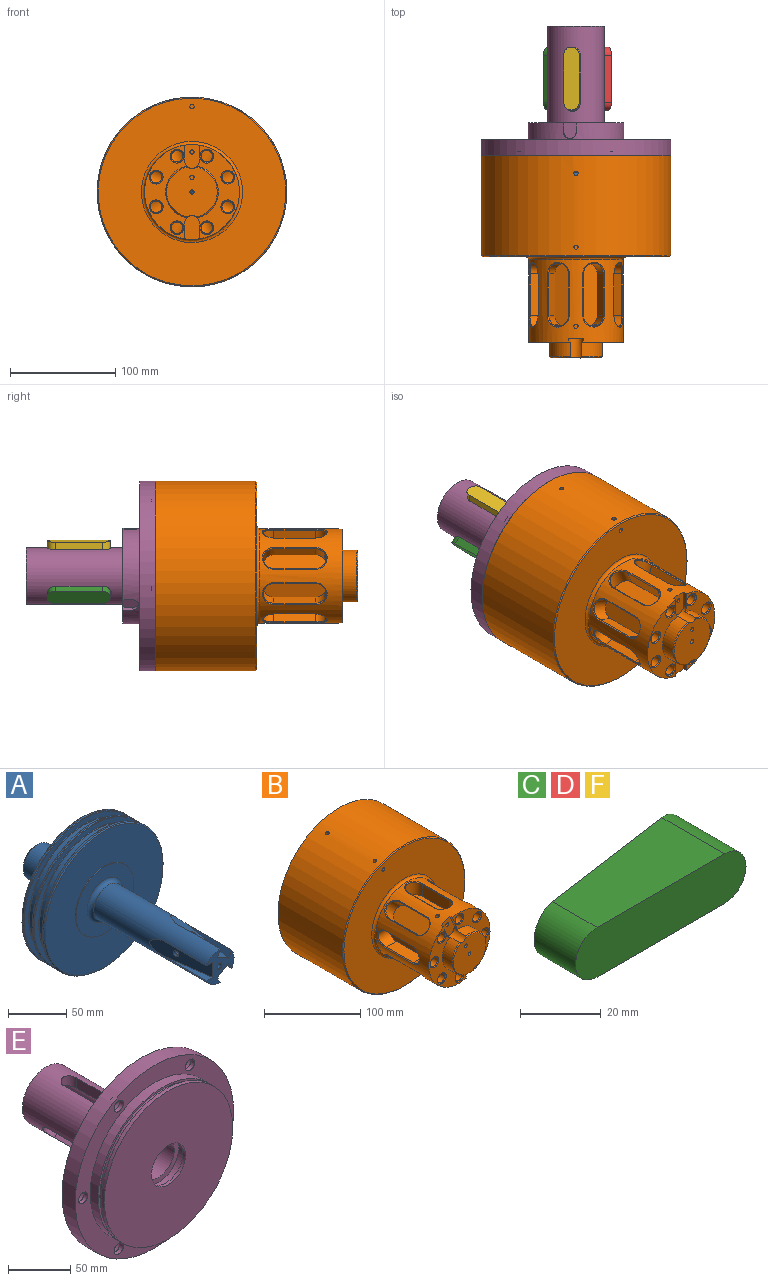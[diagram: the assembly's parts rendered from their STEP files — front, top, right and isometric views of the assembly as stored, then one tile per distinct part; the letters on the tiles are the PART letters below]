
ASSEMBLY  parts=6 mates=5
PART A: 68 faces, bbox 145x224.3x145 mm
  f0: cylinder r=1.5mm len=26.28mm, axis (0,-1,0), area 245.5mm2, adj f1,f2,f3,f4,f5,f6,f65
  f1: cylinder r=1.5mm len=11.87mm, axis (-0.99,-0.14,0), area 97.1mm2, adj f0,f4,f6,f51
  f2: cylinder r=1.5mm len=11.46mm, axis (0.5,-0.14,0.86), area 97.1mm2, adj f0,f3,f6,f55
  f3: cylinder r=1.5mm len=6.5mm, axis (-0.99,-0.14,0), area 44.4mm2, adj f0,f2,f4,f5,f6,f56
  f4: cylinder r=1.5mm len=6.81mm, axis (0.5,-0.14,0.86), area 44.4mm2, adj f0,f1,f3,f5,f6,f57
  f5: cylinder r=1.5mm len=11.46mm, axis (0.5,-0.14,-0.86), area 97.1mm2, adj f0,f3,f4,f61
  f6: cylinder r=1.5mm len=6.81mm, axis (0.5,-0.14,-0.86), area 44.4mm2, adj f0,f1,f2,f3,f4,f62
  f7: cylinder r=17.48mm len=135mm, axis (0,1,0), area 11728.8mm2, adj f8,f48,f49,f50,f52,f53,f54,f58
  f8: plane 34.95x33.06mm, normal (0,-1,0), area 511.1mm2, adj f7,f48,f49,f50,f52,f53,f54,f58
  f9: cylinder r=1.5mm len=17.25mm, axis (0,0,-1), area 153.3mm2, adj f10,f32,f36
  f10: cylinder r=17.25mm len=34.5mm, axis (0,-1,0), area 2594.2mm2, adj f9,f29,f64
  f11: cylinder r=72.5mm len=145mm, axis (0,1,0), area 774.4mm2, adj f39,f40
  f12: plane 143x143mm, normal (0,-1,0), area 12212.2mm2, adj f26,f39
  f13: plane 144x144mm, normal (0,-1,0), area 2393.1mm2, adj f42,f43
  f14: plane 144x144mm, normal (0,1,0), area 2393.1mm2, adj f40,f41
  f15: cylinder r=66mm len=132mm, axis (0,-1,0), area 3524.9mm2, adj f41,f42
  f16: cylinder r=72.5mm len=145mm, axis (0,1,0), area 728.8mm2, adj f43,f44
  f17: plane 144x144mm, normal (0,-1,0), area 2393.1mm2, adj f46,f47
  f18: plane 144x144mm, normal (0,1,0), area 2393.1mm2, adj f44,f45
  f19: cylinder r=66mm len=132mm, axis (0,-1,0), area 3524.9mm2, adj f45,f46
  f20: cylinder r=72.5mm len=145mm, axis (0,1,0), area 774.4mm2, adj f38,f47
  f21: plane 143x143mm, normal (0,1,0), area 2582.4mm2, adj f22,f38
  f22: cylinder r=65.5mm len=131mm, axis (0,-1,0), area 535mm2, adj f21,f23
  f23: plane 131x131mm, normal (0,1,0), area 3091.3mm2, adj f22,f24
  f24: cylinder r=57.5mm len=115mm, axis (0,1,0), area 2529mm2, adj f23,f25
  f25: plane 115x115mm, normal (0,1,0), area 9098.6mm2, adj f24,f64
  f26: cylinder r=35mm len=70mm, axis (0,1,0), area 219.9mm2, adj f12,f27
  f27: plane 70x70mm, normal (0,-1,0), area 2399.6mm2, adj f26,f63
  f28: cylinder r=17.48mm len=34.95mm, axis (0,1,0), area 3403.8mm2, adj f29,f31
  f29: plane 34.95x34.95mm, normal (0,-1,0), area 24.5mm2, adj f10,f28
  f30: plane 26.95x26.95mm, normal (0,1,0), area 550.8mm2, adj f31,f33
  f31: cone r=13.48mm half-angle=45deg, axis (0,-1,0), area 550mm2, adj f28,f30
  f32: cylinder r=1.5mm len=56mm, axis (0,1,0), area 518.8mm2, adj f9,f33,f35
  f33: cone r=1.5mm half-angle=45deg, axis (0,1,0), area 17.8mm2, adj f30,f32
  f34: cone r=0mm half-angle=59deg, axis (0,0,-1), area 8.2mm2, adj f35
  f35: cylinder r=1.5mm len=3mm, axis (0,0,-1), area 17.5mm2, adj f32,f34,f36
  f36: cylinder r=1.5mm len=13mm, axis (0,1,0), area 113.5mm2, adj f9,f35,f37
  f37: cone r=0mm half-angle=59deg, axis (0,1,0), area 8.2mm2, adj f36
  f38: cone r=72.5mm half-angle=45deg, axis (0,-1,0), area 639.8mm2, adj f20,f21
  f39: cone r=71.5mm half-angle=45deg, axis (0,1,0), area 639.8mm2, adj f11,f12
  f40: cone r=72.5mm half-angle=45deg, axis (0,-1,0), area 321mm2, adj f11,f14
  f41: cone r=66.5mm half-angle=45deg, axis (0,-1,0), area 294.3mm2, adj f14,f15
  f42: cone r=66mm half-angle=45deg, axis (0,1,0), area 294.3mm2, adj f13,f15
  f43: cone r=72mm half-angle=45deg, axis (0,1,0), area 321mm2, adj f13,f16
  f44: cone r=72.5mm half-angle=45deg, axis (0,-1,0), area 321mm2, adj f16,f18
  f45: cone r=66.5mm half-angle=45deg, axis (0,-1,0), area 294.3mm2, adj f18,f19
  f46: cone r=66mm half-angle=45deg, axis (0,1,0), area 294.3mm2, adj f17,f19
  f47: cone r=72mm half-angle=45deg, axis (0,1,0), area 321mm2, adj f17,f20
  f48: plane 53.99x7.59mm, normal (0,0,1), area 204.8mm2, adj f7,f8,f50
  f49: plane 53.99x7.59mm, normal (0,0,-1), area 204.8mm2, adj f7,f8,f50
  f50: plane 67.42x15.8mm, normal (-0.99,-0.14,0), area 977.6mm2, adj f7,f8,f48,f49,f51
  f51: cone r=1.5mm half-angle=45deg, axis (-0.99,-0.14,0), area 30mm2, adj f1,f50
  f52: plane 53.99x6.57mm, normal (0.87,0,-0.5), area 204.8mm2, adj f7,f8,f54
  f53: plane 53.99x6.57mm, normal (-0.87,0,0.5), area 204.8mm2, adj f7,f8,f54
  f54: plane 67.42x17.48mm, normal (0.5,-0.14,0.86), area 977.6mm2, adj f7,f8,f52,f53,f55
  f55: cone r=1.5mm half-angle=45deg, axis (0.5,-0.14,0.86), area 30mm2, adj f2,f54
  f56: cone r=0mm half-angle=59deg, axis (-0.99,-0.14,0), area 8.2mm2, adj f3
  f57: cone r=0mm half-angle=59deg, axis (0.5,-0.14,0.86), area 8.2mm2, adj f4
  f58: plane 53.99x6.57mm, normal (-0.87,0,-0.5), area 204.8mm2, adj f7,f8,f60
  f59: plane 53.99x6.57mm, normal (0.87,0,0.5), area 204.8mm2, adj f7,f8,f60
  f60: plane 67.42x17.48mm, normal (0.5,-0.14,-0.86), area 977.6mm2, adj f7,f8,f58,f59,f61
  f61: cone r=1.5mm half-angle=45deg, axis (0.5,-0.14,-0.86), area 30mm2, adj f5,f60
  f62: cone r=0mm half-angle=59deg, axis (0.5,-0.14,-0.86), area 8.2mm2, adj f6
  f63: torus R=21.48mm, axis (0,-1,0), area 747.3mm2, adj f7,f27
  f64: torus R=20.25mm, axis (0,1,0), area 543mm2, adj f10,f25
  f65: cone r=0mm half-angle=59deg, axis (0,-1,0), area 14.7mm2, adj f0,f66
  f66: cylinder r=2.5mm len=12.5mm, axis (0,-1,0), area 196.3mm2, adj f65,f67
  f67: cone r=2.5mm half-angle=45deg, axis (0,-1,0), area 12.2mm2, adj f8,f66
PART B: 156 faces, bbox 180x192x180 mm
  f0: cylinder r=2mm len=7.96mm, axis (-0.38,0,0.92), area 87.4mm2, adj f11,f123,f128
  f1: cylinder r=2mm len=41.26mm, axis (-0.38,0,0.92), area 510.5mm2, adj f2,f122,f123,f127
  f2: cylinder r=2mm len=9mm, axis (0,-1,0), area 99.3mm2, adj f1,f7,f121
  f3: cylinder r=2mm len=30mm, axis (0,-1,0), area 377mm2, adj f14,f112,f115
  f4: plane 83.39x55.54mm, normal (0,-1,0), area 1392.8mm2, adj f5,f11,f69,f80,f91,f102,f105,f106
  f5: cylinder r=25mm len=45.67mm, axis (0,1,0), area 956.4mm2, adj f4,f106,f110,f135
  f6: cylinder r=90mm len=180mm, axis (0,1,0), area 53695.6mm2, adj f9,f117,f121,f155
  f7: plane 178x178mm, normal (0,-1,0), area 17633.8mm2, adj f2,f134,f155
  f8: cylinder r=73mm len=146mm, axis (0,-1,0), area 30260.1mm2, adj f120,f132,f133
  f9: plane 180x180mm, normal (0,1,0), area 7304.2mm2, adj f6,f132,f138,f141,f144,f147,f150,f153
  f10: plane 140x140mm, normal (0,1,0), area 14318.6mm2, adj f131,f133
  f11: cylinder r=45mm len=90mm, axis (0,1,0), area 11744.7mm2, adj f0,f4,f12,f20,f21,f22,f23,f31
  f12: plane 83.39x55.54mm, normal (0,-1,0), area 1392.8mm2, adj f11,f13,f25,f36,f47,f58,f104,f106
  f13: cylinder r=25mm len=45.67mm, axis (0,1,0), area 956.4mm2, adj f12,f106,f110,f136
  f14: plane 48x48mm, normal (0,-1,0), area 1765.4mm2, adj f3,f106,f110,f111,f135,f136
  f15: cylinder r=10.1mm len=20.2mm, axis (0,0,1), area 470.9mm2, adj f16,f18,f19,f20
  f16: plane 39.8x14.84mm, normal (1,0,0), area 590.6mm2, adj f15,f17,f19,f22
  f17: cylinder r=10.1mm len=20.2mm, axis (0,0,1), area 371.8mm2, adj f16,f18,f19,f23,f24
  f18: plane 39.8x14.84mm, normal (-1,0,0), area 590.6mm2, adj f15,f17,f19,f21
  f19: plane 60x20.2mm, normal (0,0,1), area 1124.4mm2, adj f15,f16,f17,f18
  f20: bspline ~22.19x10.89mm, area 39.7mm2, adj f11,f15,f21,f22
  f21: plane 39.8x0.99mm, normal (-0.61,0,0.79), area 50mm2, adj f11,f18,f20,f23
  f22: plane 39.8x0.99mm, normal (0.61,0,0.79), area 50mm2, adj f11,f16,f20,f23
  f23: bspline ~22.18x10.89mm, area 39.7mm2, adj f11,f17,f21,f22
  f24: cylinder r=5.5mm len=14mm, axis (0,-1,0), area 483.8mm2, adj f17,f25
  f25: cone r=5.5mm half-angle=45deg, axis (0,-1,0), area 53.3mm2, adj f12,f24
  f26: cylinder r=10.1mm len=24.78mm, axis (0.71,0,0.71), area 470.9mm2, adj f27,f29,f30,f31
  f27: plane 39.8x10.49mm, normal (0.71,0,-0.71), area 590.6mm2, adj f26,f28,f30,f33
  f28: cylinder r=10.1mm len=24.78mm, axis (0.71,0,0.71), area 371.8mm2, adj f27,f29,f30,f34,f35
  f29: plane 39.8x10.49mm, normal (-0.71,0,0.71), area 590.6mm2, adj f26,f28,f30,f32
  f30: plane 60x14.28mm, normal (0.71,0,0.71), area 1124.4mm2, adj f26,f27,f28,f29
  f31: bspline ~15.69x15.69mm, area 39.7mm2, adj f11,f26,f32,f33
  f32: plane 39.8x1.25mm, normal (0.12,0,0.99), area 50mm2, adj f11,f29,f31,f34
  f33: plane 39.8x1.25mm, normal (0.99,0,0.12), area 50mm2, adj f11,f27,f31,f34
  f34: bspline ~15.69x15.69mm, area 39.7mm2, adj f11,f28,f32,f33
  f35: cylinder r=5.5mm len=14.78mm, axis (0,-1,0), area 510.7mm2, adj f28,f36
  f36: cone r=5.5mm half-angle=45deg, axis (0,-1,0), area 53.3mm2, adj f12,f35
  f37: cylinder r=10.1mm len=20.2mm, axis (1,0,0), area 470.9mm2, adj f38,f40,f41,f42
  f38: plane 39.8x14.84mm, normal (0,0,-1), area 590.6mm2, adj f37,f39,f41,f44
  f39: cylinder r=10.1mm len=20.2mm, axis (1,0,0), area 371.8mm2, adj f38,f40,f41,f45,f46
  f40: plane 39.8x14.84mm, normal (0,0,1), area 590.6mm2, adj f37,f39,f41,f43
  f41: plane 60x20.2mm, normal (1,0,0), area 1124.4mm2, adj f37,f38,f39,f40
  f42: bspline ~22.18x10.9mm, area 39.7mm2, adj f11,f37,f43,f44
  f43: plane 39.8x0.99mm, normal (0.79,0,0.61), area 50mm2, adj f11,f40,f42,f45
  f44: plane 39.8x0.99mm, normal (0.79,0,-0.61), area 50mm2, adj f11,f38,f42,f45
  f45: bspline ~22.18x10.9mm, area 39.7mm2, adj f11,f39,f43,f44
  f46: cylinder r=5.5mm len=15.63mm, axis (0,-1,0), area 540.1mm2, adj f39,f47
  f47: cone r=5.5mm half-angle=45deg, axis (0,-1,0), area 53.3mm2, adj f12,f46
  f48: cylinder r=10.1mm len=24.78mm, axis (0.71,0,-0.71), area 470.9mm2, adj f49,f51,f52,f53
  f49: plane 39.8x10.49mm, normal (-0.71,0,-0.71), area 590.6mm2, adj f48,f50,f52,f55
  f50: cylinder r=10.1mm len=24.78mm, axis (0.71,0,-0.71), area 371.9mm2, adj f49,f51,f52,f56,f57
  f51: plane 39.8x10.49mm, normal (0.71,0,0.71), area 590.6mm2, adj f48,f50,f52,f54
  f52: plane 60x14.28mm, normal (0.71,0,-0.71), area 1124.4mm2, adj f48,f49,f50,f51
  f53: bspline ~15.69x15.69mm, area 39.7mm2, adj f11,f48,f54,f55
  f54: plane 39.8x1.25mm, normal (0.99,0,-0.12), area 50mm2, adj f11,f51,f53,f56
  f55: plane 39.8x1.25mm, normal (0.12,0,-0.99), area 50mm2, adj f11,f49,f53,f56
  f56: bspline ~15.69x15.69mm, area 39.7mm2, adj f11,f50,f54,f55
  f57: cylinder r=5.5mm len=14.78mm, axis (0,-1,0), area 510.7mm2, adj f50,f58
  f58: cone r=5.5mm half-angle=45deg, axis (0,-1,0), area 53.3mm2, adj f12,f57
  f59: cylinder r=10.1mm len=20.2mm, axis (0,0,-1), area 470.9mm2, adj f60,f62,f63,f64
  f60: plane 39.8x14.84mm, normal (-1,0,0), area 590.6mm2, adj f59,f61,f63,f66
  f61: cylinder r=10.1mm len=20.2mm, axis (0,0,-1), area 371.9mm2, adj f60,f62,f63,f67,f68
  f62: plane 39.8x14.84mm, normal (1,0,0), area 590.6mm2, adj f59,f61,f63,f65
  f63: plane 60x20.2mm, normal (0,0,-1), area 1124.4mm2, adj f59,f60,f61,f62
  f64: bspline ~22.18x10.9mm, area 39.7mm2, adj f11,f59,f65,f66
  f65: plane 39.8x0.99mm, normal (0.61,0,-0.79), area 50mm2, adj f11,f62,f64,f67
  f66: plane 39.8x0.99mm, normal (-0.61,0,-0.79), area 50mm2, adj f11,f60,f64,f67
  f67: bspline ~22.18x10.9mm, area 39.7mm2, adj f11,f61,f65,f66
  f68: cylinder r=5.5mm len=14mm, axis (0,-1,0), area 483.8mm2, adj f61,f69
  f69: cone r=5.5mm half-angle=45deg, axis (0,-1,0), area 53.3mm2, adj f4,f68
  f70: cylinder r=10.1mm len=24.78mm, axis (-0.71,0,-0.71), area 470.9mm2, adj f71,f73,f74,f75
  f71: plane 39.8x10.49mm, normal (-0.71,0,0.71), area 590.6mm2, adj f70,f72,f74,f77
  f72: cylinder r=10.1mm len=24.78mm, axis (-0.71,0,-0.71), area 372mm2, adj f71,f73,f74,f78,f79
  f73: plane 39.8x10.49mm, normal (0.71,0,-0.71), area 590.6mm2, adj f70,f72,f74,f76
  f74: plane 60x14.28mm, normal (-0.71,0,-0.71), area 1124.4mm2, adj f70,f71,f72,f73
  f75: bspline ~15.69x15.69mm, area 39.7mm2, adj f11,f70,f76,f77
  f76: plane 39.8x1.25mm, normal (-0.12,0,-0.99), area 50mm2, adj f11,f73,f75,f78
  f77: plane 39.8x1.25mm, normal (-0.99,0,-0.12), area 50mm2, adj f11,f71,f75,f78
  f78: bspline ~15.69x15.69mm, area 39.7mm2, adj f11,f72,f76,f77
  f79: cylinder r=5.5mm len=14.78mm, axis (0,-1,0), area 510.7mm2, adj f72,f80
  f80: cone r=5.5mm half-angle=45deg, axis (0,-1,0), area 53.3mm2, adj f4,f79
  f81: cylinder r=10.1mm len=20.2mm, axis (-1,0,0), area 470.9mm2, adj f82,f84,f85,f86
  f82: plane 39.8x14.84mm, normal (0,0,1), area 590.6mm2, adj f81,f83,f85,f88
  f83: cylinder r=10.1mm len=20.2mm, axis (-1,0,0), area 372mm2, adj f82,f84,f85,f89,f90
  f84: plane 39.8x14.84mm, normal (0,0,-1), area 590.6mm2, adj f81,f83,f85,f87
  f85: plane 60x20.2mm, normal (-1,0,0), area 1124.4mm2, adj f81,f82,f83,f84
  f86: bspline ~22.18x10.9mm, area 39.7mm2, adj f11,f81,f87,f88
  f87: plane 39.8x0.99mm, normal (-0.79,0,-0.61), area 50mm2, adj f11,f84,f86,f89
  f88: plane 39.8x0.99mm, normal (-0.79,0,0.61), area 50mm2, adj f11,f82,f86,f89
  f89: bspline ~22.18x10.9mm, area 39.7mm2, adj f11,f83,f87,f88
  f90: cylinder r=5.5mm len=15.63mm, axis (0,-1,0), area 540.1mm2, adj f83,f91
  f91: cone r=5.5mm half-angle=45deg, axis (0,-1,0), area 53.3mm2, adj f4,f90
  f92: cylinder r=10.1mm len=24.78mm, axis (-0.71,0,0.71), area 470.9mm2, adj f93,f95,f96,f97
  f93: plane 39.8x10.49mm, normal (0.71,0,0.71), area 590.6mm2, adj f92,f94,f96,f99
  f94: cylinder r=10.1mm len=24.78mm, axis (-0.71,0,0.71), area 371.9mm2, adj f93,f95,f96,f100,f101
  f95: plane 39.8x10.49mm, normal (-0.71,0,-0.71), area 590.6mm2, adj f92,f94,f96,f98
  f96: plane 60x14.28mm, normal (-0.71,0,0.71), area 1124.4mm2, adj f92,f93,f94,f95
  f97: bspline ~15.69x15.69mm, area 39.7mm2, adj f11,f92,f98,f99
  f98: plane 39.8x1.25mm, normal (-0.99,0,0.12), area 50mm2, adj f11,f95,f97,f100
  f99: plane 39.8x1.25mm, normal (-0.12,0,0.99), area 50mm2, adj f11,f93,f97,f100
  f100: bspline ~15.69x15.69mm, area 39.7mm2, adj f11,f94,f98,f99
  f101: cylinder r=5.5mm len=14.78mm, axis (0,-1,0), area 510.7mm2, adj f94,f102
  f102: cone r=5.5mm half-angle=45deg, axis (0,-1,0), area 53.3mm2, adj f4,f101
  f103: plane 23.68x19.27mm, normal (0,-1,0), area 281.7mm2, adj f11,f104,f105,f106,f128
  f104: plane 14x5.8mm, normal (-0.92,0,-0.38), area 53mm2, adj f11,f12,f103,f106
  f105: plane 14x5.8mm, normal (0.92,0,0.38), area 53mm2, adj f4,f11,f103,f106
  f106: cylinder r=7mm len=18.5mm, axis (0,-1,0), area 246mm2, adj f4,f5,f12,f13,f14,f103,f104,f105
  f107: plane 23.68x19.27mm, normal (0,-1,0), area 294.2mm2, adj f11,f108,f109,f110
  f108: plane 14x5.8mm, normal (0.92,0,0.38), area 53mm2, adj f4,f11,f107,f110
  f109: plane 14x5.8mm, normal (-0.92,0,-0.38), area 53mm2, adj f11,f12,f107,f110
  f110: cylinder r=7mm len=18.5mm, axis (0,-1,0), area 246mm2, adj f4,f5,f12,f13,f14,f107,f108,f109
  f111: cylinder r=2mm len=56mm, axis (0,-1,0), area 703.7mm2, adj f14,f129
  f112: cylinder r=2mm len=23.7mm, axis (-0.38,0,0.92), area 271.8mm2, adj f3,f114,f123,f128
  f113: plane 4x4mm, normal (0,-1,0), area 12.6mm2, adj f114
  f114: cylinder r=2mm len=5mm, axis (0,-1,0), area 62.8mm2, adj f112,f113,f115
  f115: cylinder r=2mm len=4.77mm, axis (-0.38,0,0.92), area 19.2mm2, adj f3,f114,f116
  f116: plane 4x3.7mm, normal (-0.38,0,0.92), area 12.6mm2, adj f115
  f117: cylinder r=2mm len=9.83mm, axis (-0.38,0,0.92), area 112.8mm2, adj f6,f119,f122
  f118: plane 4x4mm, normal (0,-1,0), area 12.6mm2, adj f119
  f119: cylinder r=2mm len=5mm, axis (0,-1,0), area 62.8mm2, adj f117,f118,f120
  f120: cylinder r=2mm len=8.95mm, axis (-0.38,0,0.92), area 100.9mm2, adj f8,f119,f122
  f121: cylinder r=2mm len=9.83mm, axis (-0.38,0,0.92), area 112.8mm2, adj f2,f6,f122
  f122: cylinder r=2mm len=70mm, axis (0,-1,0), area 879.6mm2, adj f1,f117,f120,f121
  f123: cylinder r=2mm len=75mm, axis (0,-1,0), area 942.5mm2, adj f0,f1,f112,f125
  f124: plane 4x3.7mm, normal (-0.38,0,0.92), area 12.6mm2, adj f125
  f125: cylinder r=2mm len=5.15mm, axis (-0.38,0,0.92), area 31.8mm2, adj f123,f124,f127
  f126: plane 4x4mm, normal (0,-1,0), area 12.6mm2, adj f127
  f127: cylinder r=2mm len=5mm, axis (0,-1,0), area 62.8mm2, adj f1,f125,f126
  f128: cylinder r=2mm len=11.5mm, axis (0,-1,0), area 130.7mm2, adj f0,f103,f112
  f129: plane 35x35mm, normal (0,1,0), area 949.5mm2, adj f111,f130
  f130: cylinder r=17.5mm len=56mm, axis (0,1,0), area 6157.5mm2, adj f129,f131
  f131: cone r=18.5mm half-angle=14deg, axis (0,1,0), area 466.3mm2, adj f10,f130
  f132: cone r=75mm half-angle=15.9deg, axis (0,1,0), area 3384.9mm2, adj f8,f9
  f133: torus R=70mm, axis (0,-1,0), area 2129.2mm2, adj f8,f10
  f134: torus R=48mm, axis (0,-1,0), area 1364.7mm2, adj f7,f11
  f135: cone r=24mm half-angle=45deg, axis (0,1,0), area 95.8mm2, adj f5,f14,f106,f110
  f136: cone r=24mm half-angle=45deg, axis (0,1,0), area 95.8mm2, adj f13,f14,f106,f110
  f137: cylinder r=4.3mm len=36.3mm, axis (0,1,0), area 980.7mm2, adj f138,f139
  f138: cone r=4.3mm half-angle=45deg, axis (0,1,0), area 28.9mm2, adj f9,f137
  f139: cone r=0mm half-angle=59deg, axis (0,1,0), area 67.8mm2, adj f137
  f140: cylinder r=4.3mm len=36.3mm, axis (0,1,0), area 980.7mm2, adj f141,f142
  f141: cone r=4.3mm half-angle=45deg, axis (0,1,0), area 28.9mm2, adj f9,f140
  f142: cone r=0mm half-angle=59deg, axis (0,1,0), area 67.8mm2, adj f140
  f143: cylinder r=4.3mm len=36.3mm, axis (0,1,0), area 980.7mm2, adj f144,f145
  f144: cone r=4.3mm half-angle=45deg, axis (0,1,0), area 28.9mm2, adj f9,f143
  f145: cone r=0mm half-angle=59deg, axis (0,1,0), area 67.8mm2, adj f143
  f146: cylinder r=4.3mm len=36.3mm, axis (0,1,0), area 980.7mm2, adj f147,f148
  f147: cone r=4.3mm half-angle=45deg, axis (0,1,0), area 28.9mm2, adj f9,f146
  f148: cone r=0mm half-angle=59deg, axis (0,1,0), area 67.8mm2, adj f146
  f149: cylinder r=4.3mm len=36.3mm, axis (0,1,0), area 980.7mm2, adj f150,f151
  f150: cone r=4.3mm half-angle=45deg, axis (0,1,0), area 28.9mm2, adj f9,f149
  f151: cone r=0mm half-angle=59deg, axis (0,1,0), area 67.8mm2, adj f149
  f152: cylinder r=4.3mm len=36.3mm, axis (0,1,0), area 980.7mm2, adj f153,f154
  f153: cone r=4.3mm half-angle=45deg, axis (0,1,0), area 28.9mm2, adj f9,f152
  f154: cone r=0mm half-angle=59deg, axis (0,1,0), area 67.8mm2, adj f152
  f155: cone r=89mm half-angle=45deg, axis (0,1,0), area 795.3mm2, adj f6,f7
PART C: 6 faces, bbox 59.8x23x15.1 mm
  f0: cylinder r=7.55mm len=23mm, axis (0,1,0), area 536.4mm2, adj f1,f3,f4,f5
  f1: plane 44.7x21.94mm, normal (0,0,1), area 840.3mm2, adj f0,f2,f4,f5
  f2: cylinder r=7.55mm len=15.66mm, axis (0,1,0), area 355.3mm2, adj f1,f3,f4,f5
  f3: plane 44.7x21.94mm, normal (0,0,-1), area 840.3mm2, adj f0,f2,f4,f5
  f4: plane 59.8x15.1mm, normal (0,-1,0), area 854mm2, adj f0,f1,f2,f3
  f5: plane 59.8x15.1mm, normal (-0.14,0.99,0), area 862.4mm2, adj f0,f1,f2,f3
PART D: same geometry as C
PART E: 68 faces, bbox 180x139x180 mm
  f0: cylinder r=72.95mm len=145.9mm, axis (0,1,0), area 1604.3mm2, adj f5,f63
  f1: cylinder r=72.95mm len=145.9mm, axis (0,1,0), area 4125.2mm2, adj f3,f65
  f2: cylinder r=90mm len=180mm, axis (0,1,0), area 8482.3mm2, adj f3,f4
  f3: plane 180x180mm, normal (0,-1,0), area 8208.7mm2, adj f1,f2,f45,f48,f51,f54,f57,f60
  f4: plane 180x180mm, normal (0,1,0), area 17581.1mm2, adj f2,f6,f47,f50,f53,f56,f59,f62
  f5: plane 145.9x145.9mm, normal (0,-1,0), area 15533.2mm2, adj f0,f10
  f6: cylinder r=45.5mm len=91mm, axis (0,-1,0), area 4071.4mm2, adj f4,f7,f33,f34,f35,f37,f38,f39
  f7: plane 91x90.59mm, normal (0,1,0), area 2717.1mm2, adj f6,f31,f33,f35,f36,f37,f39,f40
  f8: plane 54x54mm, normal (0,1,0), area 1286.5mm2, adj f9,f12,f14,f16,f18
  f9: cylinder r=27mm len=96mm, axis (0,-1,0), area 13654.1mm2, adj f8,f19,f20,f21,f22,f23,f24,f25
  f10: cylinder r=19.43mm len=38.85mm, axis (0,-1,0), area 366.2mm2, adj f5,f66
  f11: plane 45x45mm, normal (0,-1,0), area 628.3mm2, adj f12,f67
  f12: cylinder r=17.5mm len=128mm, axis (0,1,0), area 11393mm2, adj f8,f11,f19,f20,f21,f22,f23,f24
  f13: cone r=0mm half-angle=59deg, axis (0,1,0), area 16.2mm2, adj f14
  f14: cylinder r=2.1mm len=20mm, axis (0,1,0), area 263.9mm2, adj f8,f13
  f15: cone r=0mm half-angle=59deg, axis (0,1,0), area 16.2mm2, adj f16
  f16: cylinder r=2.1mm len=20mm, axis (0,1,0), area 263.9mm2, adj f8,f15
  f17: cone r=0mm half-angle=59deg, axis (0,1,0), area 16.2mm2, adj f18
  f18: cylinder r=2.1mm len=20mm, axis (0,1,0), area 263.9mm2, adj f8,f17
  f19: cylinder r=7.5mm len=18.58mm, axis (-0.87,0,0.5), area 232.9mm2, adj f9,f12,f20,f22
  f20: plane 46.23x8.77mm, normal (0.5,0,0.87), area 468.1mm2, adj f9,f12,f19,f21
  f21: cylinder r=7.5mm len=18.59mm, axis (-0.87,0,0.5), area 231.1mm2, adj f9,f12,f20,f22
  f22: plane 45.59x8.77mm, normal (-0.5,0,-0.87), area 461.6mm2, adj f9,f12,f19,f21
  f23: cylinder r=7.5mm len=18.58mm, axis (0.87,0,0.5), area 232.9mm2, adj f9,f12,f24,f26
  f24: plane 46.23x8.77mm, normal (0.5,0,-0.87), area 468.1mm2, adj f9,f12,f23,f25
  f25: cylinder r=7.5mm len=18.59mm, axis (0.87,0,0.5), area 231.1mm2, adj f9,f12,f24,f26
  f26: plane 45.59x8.78mm, normal (-0.5,0,0.87), area 461.6mm2, adj f9,f12,f23,f25
  f27: cylinder r=7.5mm len=15mm, axis (0,0,-1), area 232.9mm2, adj f9,f12,f28,f30
  f28: plane 46.23x10.13mm, normal (-1,0,0), area 468.1mm2, adj f9,f12,f27,f29
  f29: cylinder r=7.5mm len=15mm, axis (0,0,-1), area 231mm2, adj f9,f12,f28,f30
  f30: plane 45.59x10.13mm, normal (1,0,0), area 461.6mm2, adj f9,f12,f27,f29
  f31: cylinder r=34mm len=68mm, axis (0,1,0), area 854.5mm2, adj f7,f32
  f32: plane 68x68mm, normal (0,1,0), area 1341.5mm2, adj f9,f31
  f33: plane 8.9x3.43mm, normal (0.5,0,0.87), area 35.3mm2, adj f6,f7,f34,f36
  f34: cylinder r=6.1mm len=12.75mm, axis (-0.87,0,0.5), area 79.9mm2, adj f6,f33,f35,f36
  f35: plane 8.9x3.43mm, normal (-0.5,0,-0.87), area 35.3mm2, adj f6,f7,f34,f36
  f36: plane 15x10.57mm, normal (0.87,0,-0.5), area 167mm2, adj f7,f33,f34,f35
  f37: plane 8.9x3.96mm, normal (-1,0,0), area 35.3mm2, adj f6,f7,f38,f40
  f38: cylinder r=6.1mm len=12.2mm, axis (0,0,-1), area 79.9mm2, adj f6,f37,f39,f40
  f39: plane 8.9x3.96mm, normal (1,0,0), area 35.3mm2, adj f6,f7,f38,f40
  f40: plane 15x12.2mm, normal (0,0,1), area 167mm2, adj f7,f37,f38,f39
  f41: plane 8.9x3.43mm, normal (0.5,0,-0.87), area 35.3mm2, adj f6,f7,f42,f44
  f42: cylinder r=6.1mm len=12.75mm, axis (0.87,0,0.5), area 79.9mm2, adj f6,f41,f43,f44
  f43: plane 8.9x3.43mm, normal (-0.5,0,0.87), area 35.3mm2, adj f6,f7,f42,f44
  f44: plane 15x10.57mm, normal (-0.87,0,-0.5), area 167mm2, adj f7,f41,f42,f43
  f45: cylinder r=5.25mm len=10.5mm, axis (0,1,0), area 131.9mm2, adj f3,f46
  f46: plane 17x17mm, normal (0,1,0), area 140.4mm2, adj f45,f47
  f47: cylinder r=8.5mm len=17mm, axis (0,1,0), area 587.5mm2, adj f4,f46
  f48: cylinder r=5.25mm len=10.5mm, axis (0,1,0), area 131.9mm2, adj f3,f49
  f49: plane 17x17mm, normal (0,1,0), area 140.4mm2, adj f48,f50
  f50: cylinder r=8.5mm len=17mm, axis (0,1,0), area 587.5mm2, adj f4,f49
  f51: cylinder r=5.25mm len=10.5mm, axis (0,1,0), area 131.9mm2, adj f3,f52
  f52: plane 17x17mm, normal (0,1,0), area 140.4mm2, adj f51,f53
  f53: cylinder r=8.5mm len=17mm, axis (0,1,0), area 587.5mm2, adj f4,f52
  f54: cylinder r=5.25mm len=10.5mm, axis (0,1,0), area 131.9mm2, adj f3,f55
  f55: plane 17x17mm, normal (0,1,0), area 140.4mm2, adj f54,f56
  f56: cylinder r=8.5mm len=17mm, axis (0,1,0), area 587.5mm2, adj f4,f55
  f57: cylinder r=5.25mm len=10.5mm, axis (0,1,0), area 131.9mm2, adj f3,f58
  f58: plane 17x17mm, normal (0,1,0), area 140.4mm2, adj f57,f59
  f59: cylinder r=8.5mm len=17mm, axis (0,1,0), area 587.5mm2, adj f4,f58
  f60: cylinder r=5.25mm len=10.5mm, axis (0,1,0), area 131.9mm2, adj f3,f61
  f61: plane 17x17mm, normal (0,1,0), area 140.4mm2, adj f60,f62
  f62: cylinder r=8.5mm len=17mm, axis (0,1,0), area 587.5mm2, adj f4,f61
  f63: plane 145.9x145.9mm, normal (0,1,0), area 904.2mm2, adj f0,f64
  f64: cylinder r=70.95mm len=141.9mm, axis (0,-1,0), area 1560.3mm2, adj f63,f65
  f65: plane 145.9x145.9mm, normal (0,-1,0), area 904.2mm2, adj f1,f64
  f66: plane 45x45mm, normal (0,1,0), area 405mm2, adj f10,f67
  f67: cylinder r=22.5mm len=45mm, axis (0,1,0), area 1131mm2, adj f11,f66
PART F: same geometry as C
PLACE A rot(axis=(0.2,0,0.98),180deg) t=(-2.66,142.75,-25.97)mm
PLACE B rot(axis=(0,1,0),22.5deg) t=(-2.66,116,-25.97)mm fixed
PLACE C rot(axis=(0.69,0.69,0.23),153.7deg) t=(-10.9,270.71,-32.3)mm
PLACE D rot(axis=(0.19,0.19,0.96),92.2deg) t=(6.94,270.71,-29.95)mm
PLACE E rot(axis=(0,1,0),112.5deg) t=(-2.66,207,-25.97)mm
PLACE F rot(axis=(-0.6,-0.6,0.53),124.4deg) t=(-4.02,270.71,-15.67)mm
MATE fastened E.f10 <-> B.f5  axis (0,-1,0) through (-2.66,192,-25.97)mm
MATE slider A.f28 <-> B.f111  axis (0,-1,0) through (-2.66,107.25,-25.97)mm
MATE slider C.f0 <-> E.f19  axis (0.79,0,0.61) through (-19.97,287.5,-39.26)mm
MATE slider D.f0 <-> E.f27  axis (-0.92,0,0.38) through (17.5,287.5,-34.32)mm
MATE slider F.f0 <-> E.f23  axis (0.13,0,-0.99) through (-4,287.5,-15.81)mm
